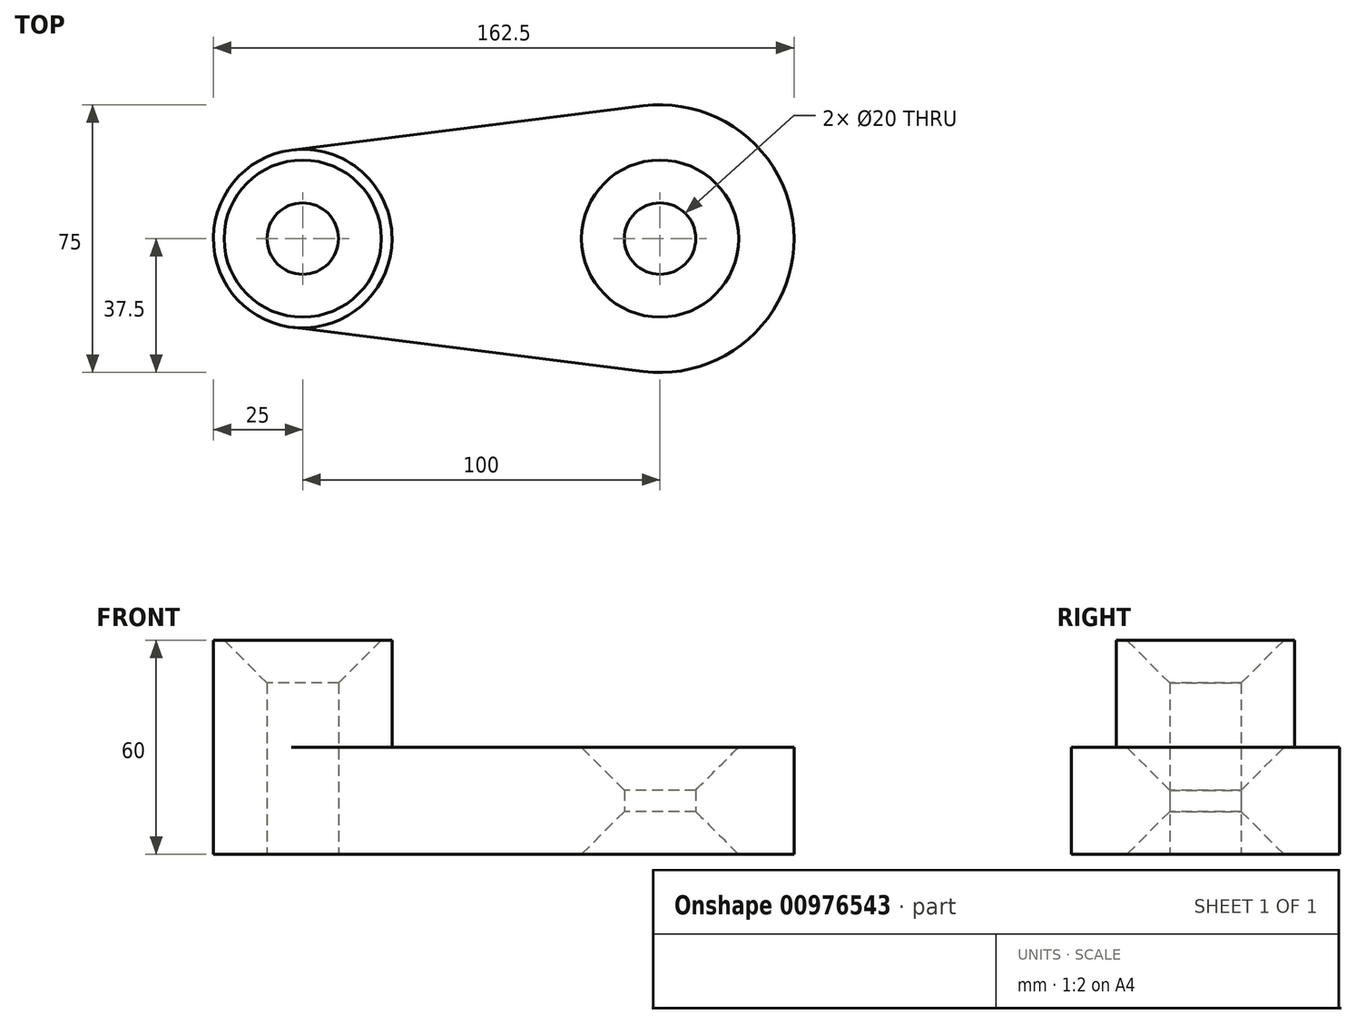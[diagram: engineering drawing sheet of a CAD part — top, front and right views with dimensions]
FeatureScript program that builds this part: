
annotation { "Feature Type Name" : "Feature", "Feature Type Description" : "" }
export const myFeature = defineFeature(function(context is Context, id is Id, definition is map)
    precondition{}
    {
        {
            var Q0;
            Q0=qCreatedBy(makeId("Top.planeOp"),FACE);
            var sketch = newSketch(context, id + "F0", { "sketchPlane" : qUnion([Q0])});
            skCircle(sketch, "E0", {"center": v(0, 0) * mm, "radius": 25 * mm});
            skCircle(sketch, "E1", {"center": v(100, 0) * mm, "radius": 37.5 * mm});
            skLineSegment(sketch, "E2", {"start": v(-3.12, 24.8) * mm, "end": v(95.31, 37.2) * mm});
            skLineSegment(sketch, "E3", {"start": v(-3.13, -24.8) * mm, "end": v(95.31, -37.2) * mm});
            skCircle(sketch, "E4", {"center": v(0, 0) * mm, "radius": 10 * mm});
            skCircle(sketch, "E5", {"center": v(100, 0) * mm, "radius": 10 * mm});
            skSolve(sketch);
        }
        {
            var Q0;
            Q0=makeQuery(id+"F0.imprint","IMPRINT",FACE,{"disambiguationData":[TD([[makeQuery(id+"F0.imprint","IMPRINT",EDGE,{"derivedFrom":sQuery(id+"F0.wireOp",EDGE,"E4")}),-1.0]])]});
            var Q1;
            Q1=makeQuery(id+"F0.imprint","IMPRINT",FACE,{"disambiguationData":[TD([[makeQuery(id+"F0.imprint","IMPRINT",EDGE,{"derivedFrom":sQuery(id+"F0.wireOp",EDGE,"E5")}),-1.0]])]});
            var Q2;
            {var subQ0=sQuery(id+"F0.wireOp",EDGE,"E2");Q2=makeQuery(id+"F0.imprint","IMPRINT",FACE,{"disambiguationData":[TD([[makeQuery(id+"F0.imprint","IMPRINT",EDGE,{"derivedFrom":subQ0}),-1.0]])]});}
            extrude(context, id + "F1", {"entities" : qUnion([Q0, Q1, Q2]), "depth" : 30 * mm, "offsetDistance" : 25 * mm});
        }
        {
            var Q0;
            Q0=makeQuery(id+"F0.imprint","IMPRINT",FACE,{"disambiguationData":[TD([[makeQuery(id+"F0.imprint","IMPRINT",EDGE,{"derivedFrom":sQuery(id+"F0.wireOp",EDGE,"E4")}),-1.0]])]});
            extrude(context, id + "F2", {"entities" : qUnion([Q0]), "operationType" : NewBodyOperationType.ADD, "depth" : 60 * mm, "offsetDistance" : 25 * mm});
        }
        {
            var Q0;
            Q0=makeQuery(id+"F2.opExtrude","CAP_EDGE",EDGE,{"disambiguationData":[OSD([sQuery(id+"F0.wireOp",EDGE,"E4")])],"isStart":false});
            chamfer(context, id + "F3", {"entities" : qUnion([Q0]), "width" : 12 * mm, "tangentPropagation" : true});
        }
        {
            var Q0;
            Q0=makeQuery(id+"F1.opExtrude","CAP_EDGE",EDGE,{"disambiguationData":[OSD([sQuery(id+"F0.wireOp",EDGE,"E5")])],"isStart":true});
            var Q1;
            Q1=makeQuery(id+"F1.opExtrude","CAP_EDGE",EDGE,{"disambiguationData":[OSD([sQuery(id+"F0.wireOp",EDGE,"E5")])],"isStart":false});
            var Q2;
            Q2=makeQuery(id+"F1.opExtrude","CAP_EDGE",EDGE,{"disambiguationData":[OSD([sQuery(id+"F0.wireOp",EDGE,"E4")])],"isStart":false});
            chamfer(context, id + "F4", {"entities" : qUnion([Q0, Q1, Q2]), "width" : 12 * mm, "tangentPropagation" : true});
        }
    });
